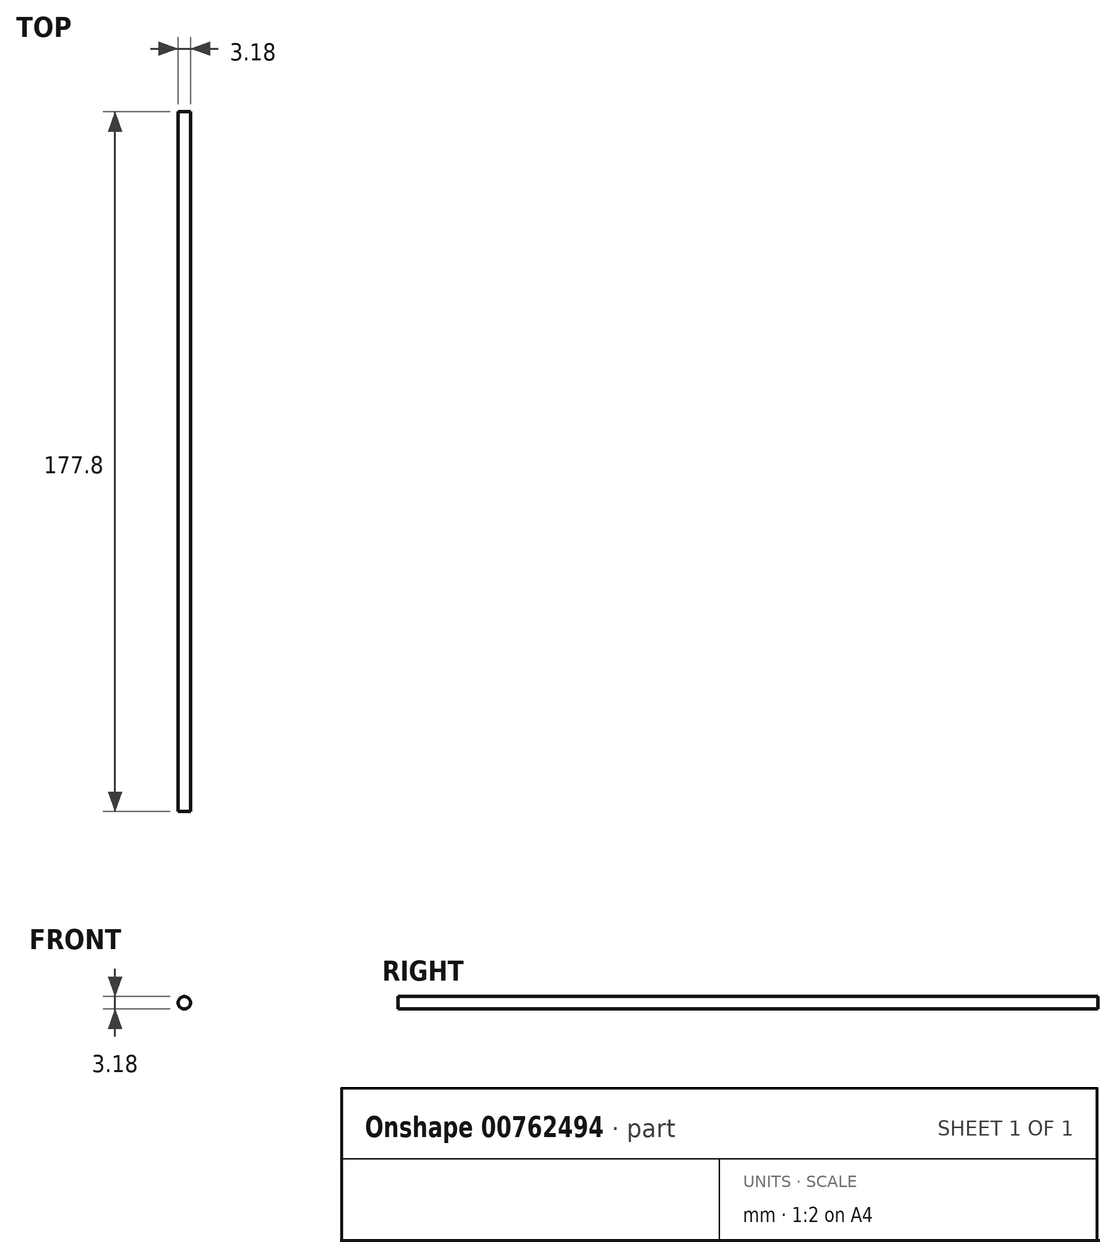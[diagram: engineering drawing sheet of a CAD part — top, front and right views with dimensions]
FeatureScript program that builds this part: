
annotation { "Feature Type Name" : "Feature", "Feature Type Description" : "" }
export const myFeature = defineFeature(function(context is Context, id is Id, definition is map)
    precondition{}
    {
        {
            var Q0;
            Q0=qCreatedBy(makeId("Front.planeOp"),FACE);
            var sketch = newSketch(context, id + "F0", { "sketchPlane" : qUnion([Q0])});
            skCircle(sketch, "E0", {"center": v(0, 0) * mm, "radius": 1.59 * mm});
            skSolve(sketch);
        }
        {
            var Q0;
            Q0 = qSketchRegion(id + "F0", true);
            extrude(context, id + "F1", {"entities" : qUnion([Q0]), "depth" : 177.8 * mm, "offsetDistance" : 25.4 * mm});
        }
    });
